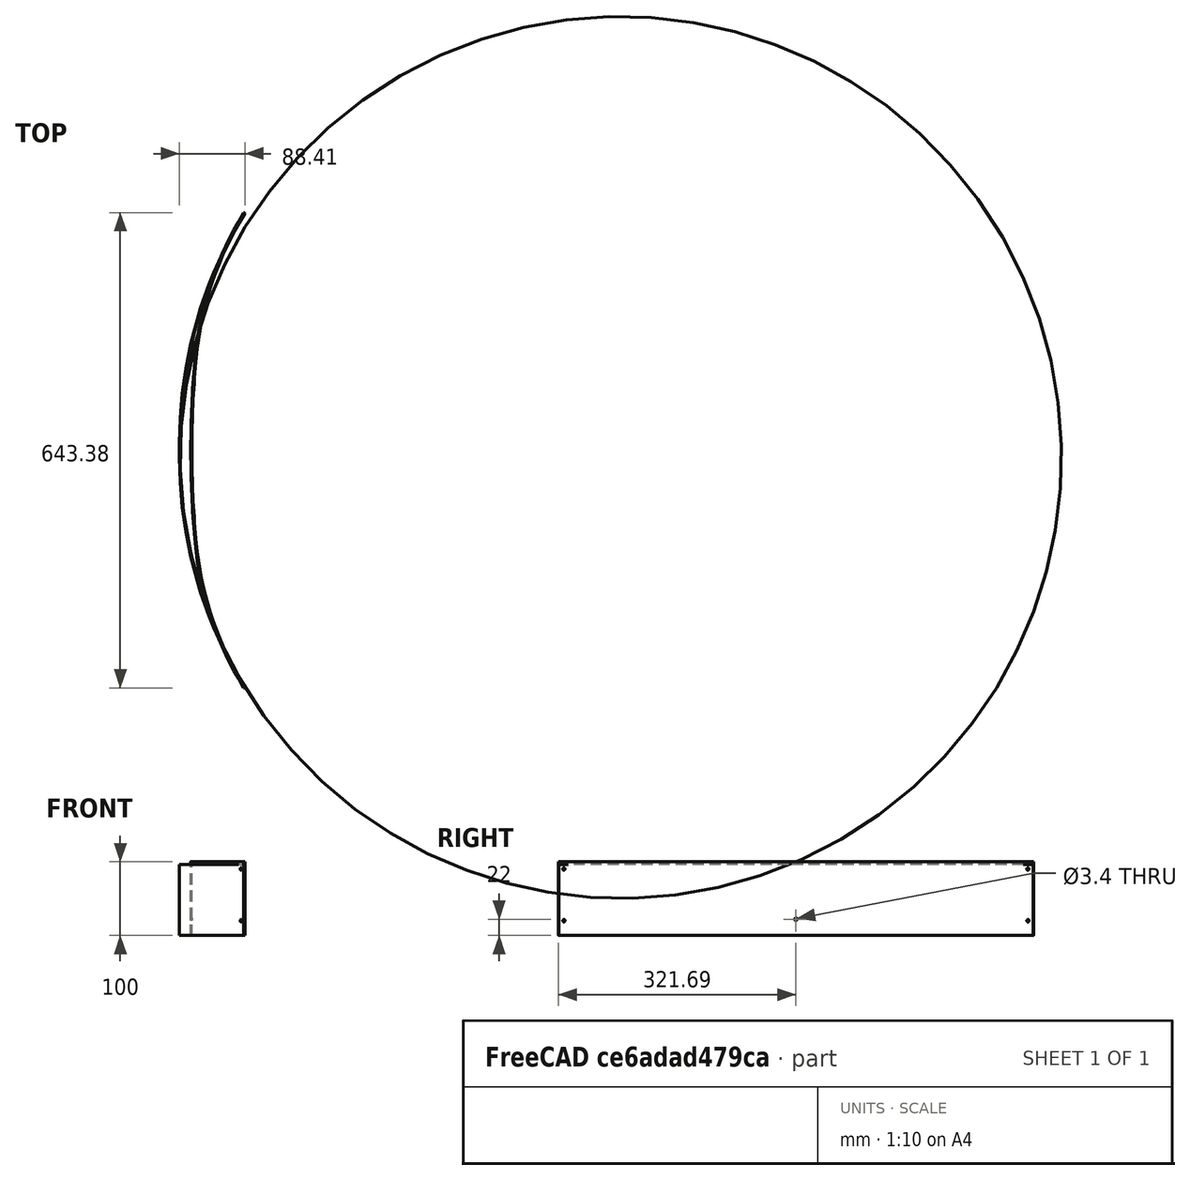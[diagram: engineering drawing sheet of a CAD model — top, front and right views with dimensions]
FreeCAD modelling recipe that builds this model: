
FCSTD DOCUMENT  (FreeCAD 1.1R38827 (Git))
Label: composit_stand3_hat_plexiglass_model
License: All rights reserved
LicenseURL: http://en.wikipedia.org/wiki/All_rights_reserved
objects: App::Link×1, PartDesign::SubShapeBinder×1, PartDesign::FeaturePython×1, Part::Feature×1, PartDesign::CoordinateSystem×1, PartDesign::Body×1
note: 6 computed .brp shape members not serialized (recipe doc carries the construction recipe); baked Part::Feature solids carry a one-line shape summary decoded from their .brp
EXTERNAL_REF file=composit_stand3_hat_plexiglass_main.FCStd obj=Sketch

FEATURE [App::Link] Link  label="main_sketch"
  LinkedObject = -> <external composit_stand3_hat_plexiglass_main.FCStd>#Sketch
FEATURE [PartDesign::SubShapeBinder] Binder
  BindCopyOnChange = 0
  BindMode = 0
  ClaimChildren = false
  Context = -> Body [Binder.]
  Fuse = false
  MakeFace = true
  OffsetFill = false
  OffsetIntersection = false
  OffsetJoinType = 0
  OffsetOpenResult = false
  PartialLoad = false
  Relative = true
  Support = -> [Link]
  _Version = 2
FEATURE [PartDesign::FeaturePython] BaseBend  # WARN: FeaturePython — macro-defined, semantics opaque (R4)
  BendSide = 0
  BendSketch = -> Binder
  MidPlane = false
  Reverse = false
  Suppressed = false
  length = 96
  radius = 596.406
  thickness = 1
  expr: radius = <<main_sketch>>.Constraints.r
FEATURE [Part::Feature] Body172  label="hat3_plexiglass001"
  Placement = pos=(0,0,0) rot=(0,0,1;-0.523599rad)
  shape: bbox 73.12 x 643.4 x 100 mm, 43 faces (baked)
FEATURE [PartDesign::CoordinateSystem] Local_CS
  AttacherType = Attacher::AttachEngine3D
  AttachmentOffset = pos=(0,0,6) rot=(0,0,1;0rad)
  AttachmentSupport = -> [XY_Plane]
  MapMode = 5
  Placement = pos=(0,0,6) rot=(0,0,1;0rad)
FEATURE [PartDesign::Body] Body  label="hat_plexiglass"
  AllowCompound = false
  Group = -> [Binder,BaseBend,Local_CS]
  Origin = -> Origin
  Tip = -> BaseBend
